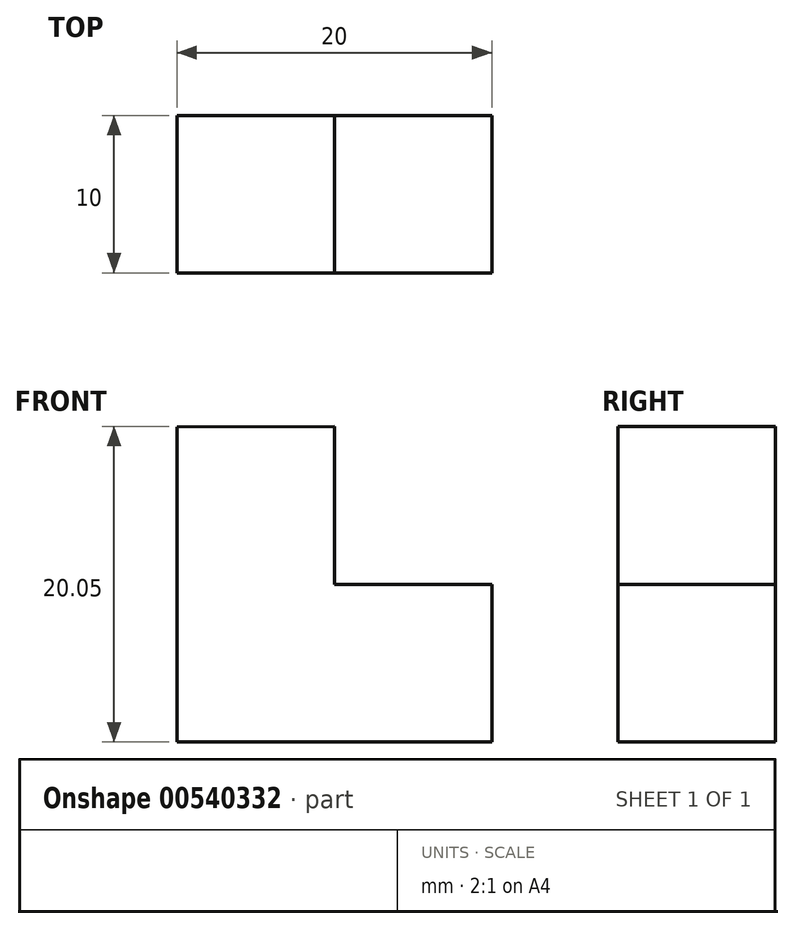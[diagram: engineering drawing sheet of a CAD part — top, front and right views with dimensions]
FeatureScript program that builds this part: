
annotation { "Feature Type Name" : "Feature", "Feature Type Description" : "" }
export const myFeature = defineFeature(function(context is Context, id is Id, definition is map)
    precondition{}
    {
        {
            var Q0;
            Q0=qCreatedBy(makeId("Front.planeOp"),FACE);
            var sketch = newSketch(context, id + "F0", { "sketchPlane" : qUnion([Q0])});
            skLineSegment(sketch, "E0", {"start": v(-15.78, 45.12) * mm, "end": v(-15.78, 25.12) * mm});
            skLineSegment(sketch, "E1", {"start": v(4.22, 25.12) * mm, "end": v(-15.78, 25.12) * mm});
            skLineSegment(sketch, "E2", {"start": v(4.22, 25.12) * mm, "end": v(4.22, 35.12) * mm});
            skLineSegment(sketch, "E3", {"start": v(4.22, 35.12) * mm, "end": v(-5.78, 35.12) * mm});
            skLineSegment(sketch, "E4", {"start": v(-5.78, 35.12) * mm, "end": v(-5.78, 45.17) * mm});
            skLineSegment(sketch, "E5", {"start": v(-5.78, 45.17) * mm, "end": v(-15.78, 45.12) * mm});
            skSolve(sketch);
        }
        {
            var Q0;
            Q0 = qSketchRegion(id + "F0", true);
            extrude(context, id + "F1", {"entities" : qUnion([Q0]), "depth" : 10 * mm, "offsetDistance" : 25 * mm});
        }
    });
